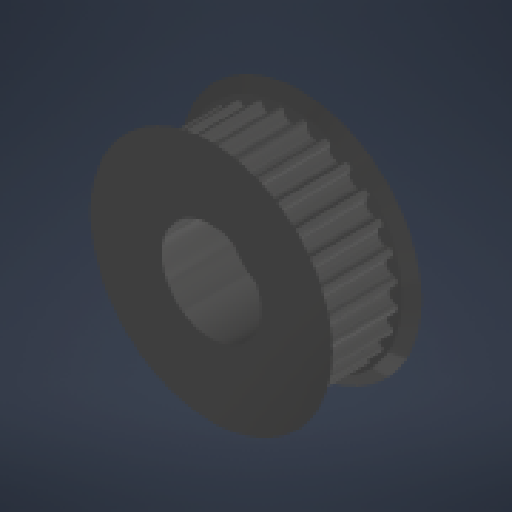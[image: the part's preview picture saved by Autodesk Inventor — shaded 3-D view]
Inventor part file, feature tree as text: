
AUTODESK INVENTOR PART (.ipt)
format: ipt  version: 2024.2 (Build 282272000, 272)  size: 377,344 bytes
history: native  units: in
note: dims shown in document units (in); Inventor stores cm internally (conversion verified against a paired STEP export)
features: other x2, extrude x2, plane x2, sketch x2
ambient origin geometry x8: Origin, YZ Plane, XZ Plane, XY Plane, X Axis, Y Axis, Z Axis, Center Point
bodies: Solid1 (feature_tree)
feature tree (8):
  other  "Thin_28T.step"
  extrude  "Extrusion1"  Depth=1.0in TaperAngle=0.0deg
  plane  "Work Plane1"
  plane  "Work Plane2"
  extrude  "Extrusion2"  Depth=0.1181in TaperAngle=0.0deg
  sketch  "Sketch1"  dims[d0=0.4803in d1=1.0in d2=0.0in]
  sketch  "Sketch3"  dims[d7=0.1575in d8=0.1181in d9=0.0in]
  other  "[LS] Pulley HTD3 28T"
